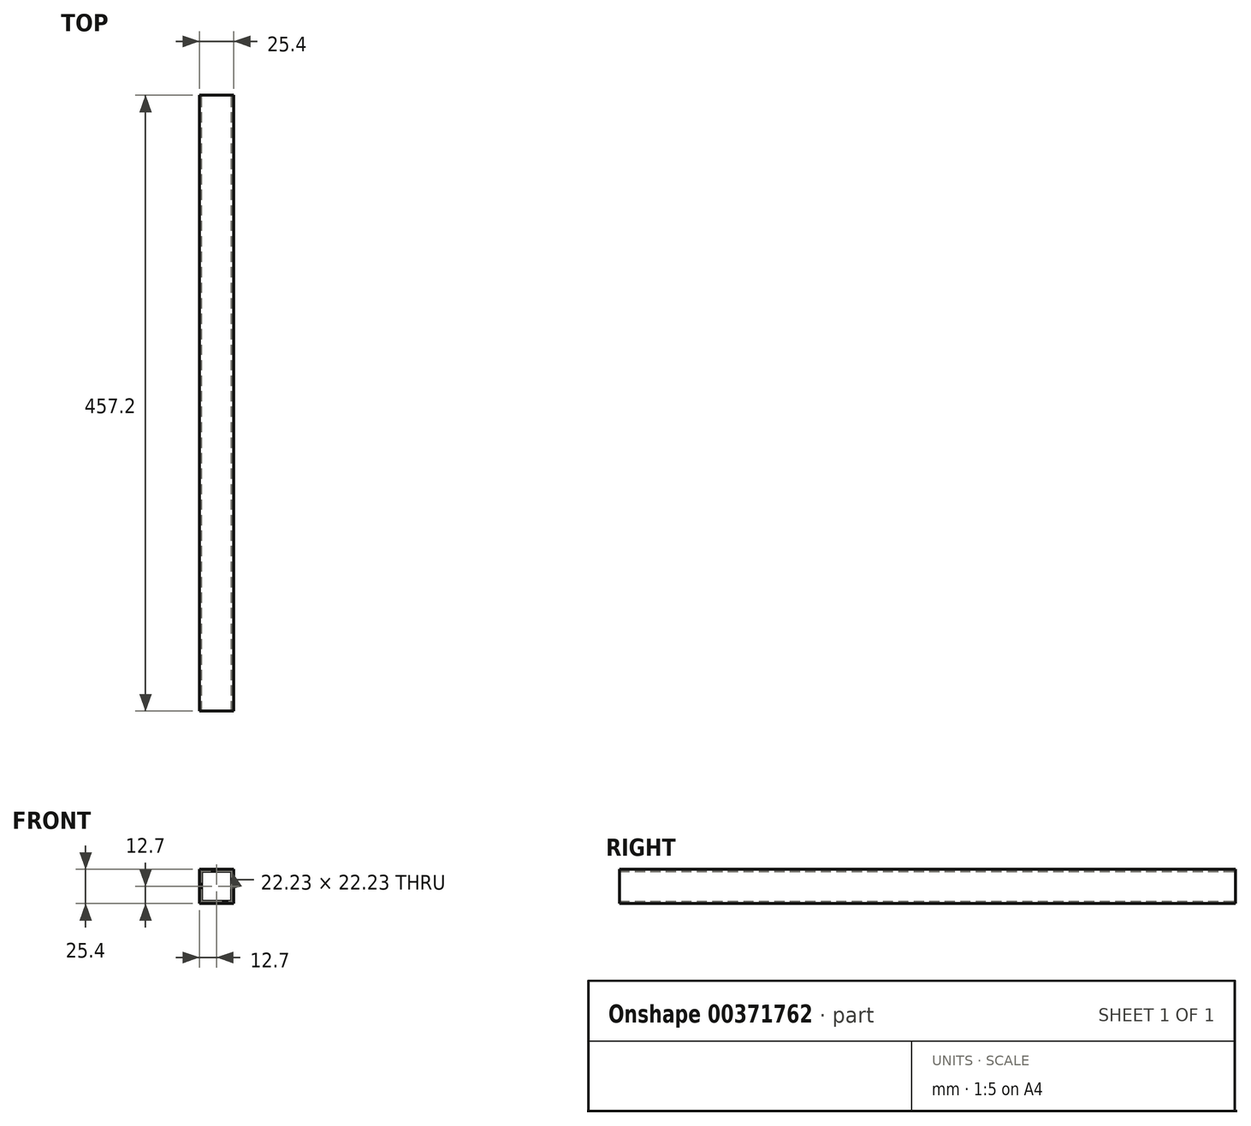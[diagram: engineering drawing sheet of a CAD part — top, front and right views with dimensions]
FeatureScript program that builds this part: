
annotation { "Feature Type Name" : "Feature", "Feature Type Description" : "" }
export const myFeature = defineFeature(function(context is Context, id is Id, definition is map)
    precondition{}
    {
        {
            var Q0;
            Q0=qCreatedBy(makeId("Front.planeOp"),FACE);
            var sketch = newSketch(context, id + "F0", { "sketchPlane" : qUnion([Q0])});
            skLineSegment(sketch, "E0.bottom", {"start": v(0, 0) * mm, "end": v(25.4, 0) * mm});
            skLineSegment(sketch, "E0.top", {"start": v(0, 25.4) * mm, "end": v(25.4, 25.4) * mm});
            skLineSegment(sketch, "E0.left", {"start": v(0, 0) * mm, "end": v(0, 25.4) * mm});
            skLineSegment(sketch, "E0.right", {"start": v(25.4, 0) * mm, "end": v(25.4, 25.4) * mm});
            skLineSegment(sketch, "E1.bottom", {"start": v(23.81, 1.59) * mm, "end": v(1.59, 1.59) * mm});
            skLineSegment(sketch, "E1.top", {"start": v(23.81, 23.81) * mm, "end": v(1.59, 23.81) * mm});
            skLineSegment(sketch, "E1.left", {"start": v(23.81, 1.59) * mm, "end": v(23.81, 23.81) * mm});
            skLineSegment(sketch, "E1.right", {"start": v(1.59, 1.59) * mm, "end": v(1.59, 23.81) * mm});
            skPoint(sketch, "E1.middle", {"position": v(12.7, 12.7) * mm});
            skSolve(sketch);
        }
        {
            var Q0;
            Q0 = qSketchRegion(id + "F0", true);
            extrude(context, id + "F1", {"entities" : qUnion([Q0]), "depth" : 457.2 * mm});
        }
    });
